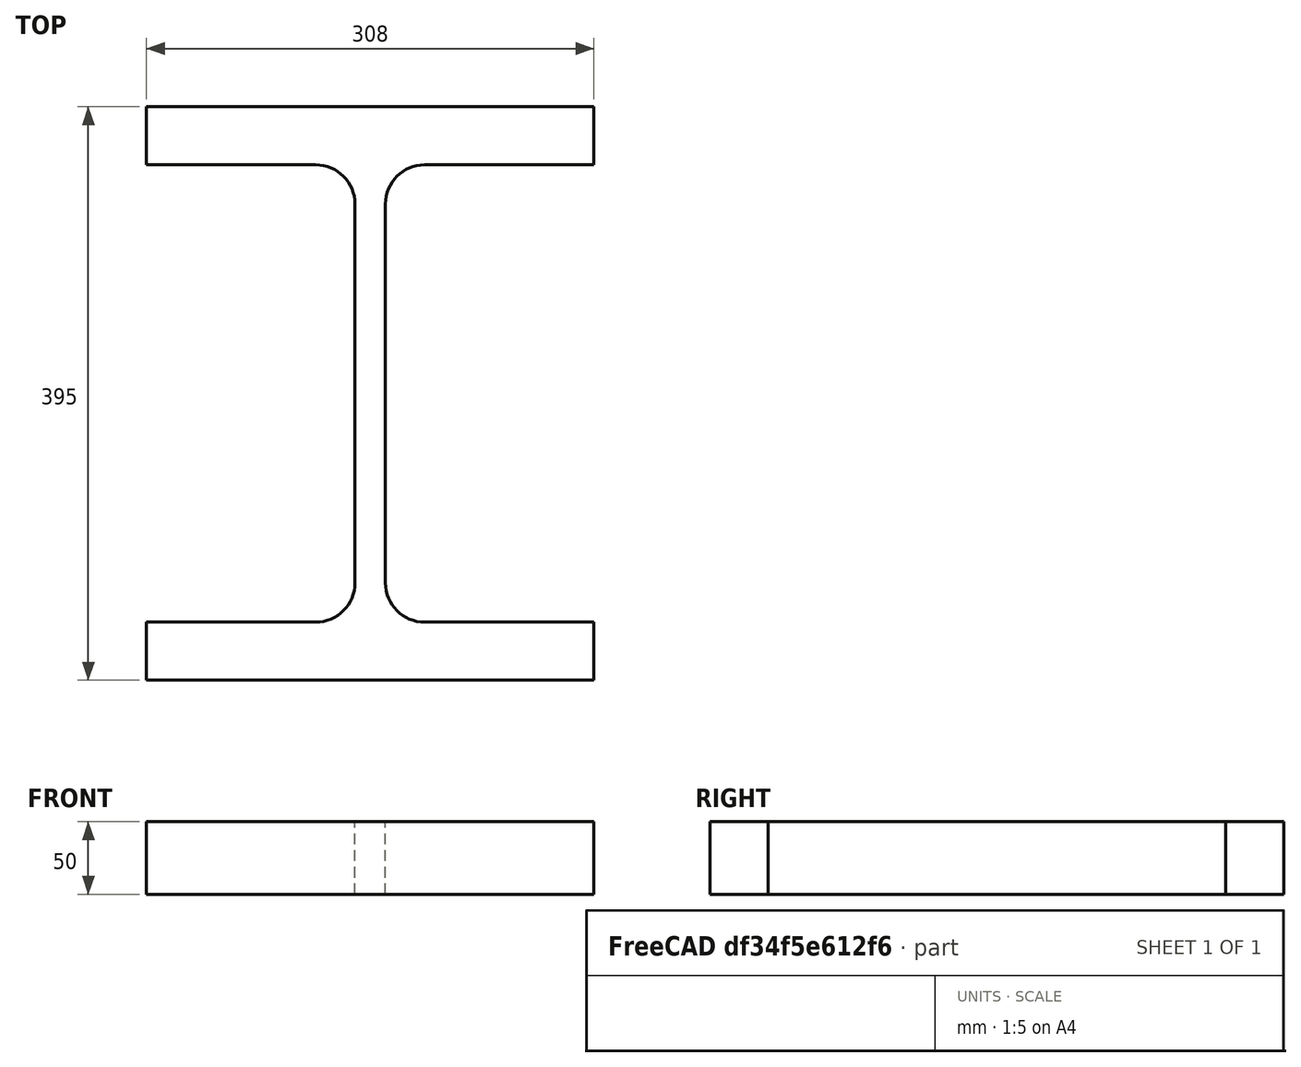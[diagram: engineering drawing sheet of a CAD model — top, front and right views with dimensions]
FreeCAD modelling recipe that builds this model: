
FCSTD DOCUMENT  (FreeCAD 0.15R4671 (Git))
Label: HE-M-Profile 360 DIN1025-4 S235JR
License: All rights reserved
LicenseURL: http://en.wikipedia.org/wiki/All_rights_reserved
objects: Sketcher::SketchObject×1, Part::Extrusion×1
note: 2 computed .brp shape members not serialized (recipe doc carries the construction recipe); baked Part::Feature solids carry a one-line shape summary decoded from their .brp

FEATURE [Sketcher::SketchObject] Sketch
  sketch-geometry (16):
    g0: LineSegment StartX=10.5 StartY=-130.5 StartZ=0 EndX=10.5 EndY=130.5 EndZ=0
    g1: LineSegment StartX=37.5 StartY=157.5 StartZ=0 EndX=154 EndY=157.5 EndZ=0
    g2: LineSegment StartX=154 StartY=157.5 StartZ=0 EndX=154 EndY=197.5 EndZ=0
    g3: LineSegment StartX=154 StartY=197.5 StartZ=0 EndX=-154 EndY=197.5 EndZ=0
    g4: LineSegment StartX=-154 StartY=197.5 StartZ=0 EndX=-154 EndY=157.5 EndZ=0
    g5: LineSegment StartX=-154 StartY=157.5 StartZ=0 EndX=-37.5 EndY=157.5 EndZ=0
    g6: LineSegment StartX=-10.5 StartY=130.5 StartZ=0 EndX=-10.5 EndY=-130.5 EndZ=0
    g7: LineSegment StartX=-37.5 StartY=-157.5 StartZ=0 EndX=-154 EndY=-157.5 EndZ=0
    g8: LineSegment StartX=-154 StartY=-157.5 StartZ=0 EndX=-154 EndY=-197.5 EndZ=0
    g9: LineSegment StartX=-154 StartY=-197.5 StartZ=0 EndX=154 EndY=-197.5 EndZ=0
    g10: LineSegment StartX=154 StartY=-197.5 StartZ=0 EndX=154 EndY=-157.5 EndZ=0
    g11: LineSegment StartX=154 StartY=-157.5 StartZ=0 EndX=37.5 EndY=-157.5 EndZ=0
    g12: ArcOfCircle CenterX=37.5 CenterY=130.5 CenterZ=0 NormalX=0 NormalY=0 NormalZ=1 Radius=27 StartAngle=1.5708 EndAngle=3.14159
    g13: ArcOfCircle CenterX=37.5 CenterY=-130.5 CenterZ=0 NormalX=0 NormalY=0 NormalZ=1 Radius=27 StartAngle=3.14159 EndAngle=4.71239
    g14: ArcOfCircle CenterX=-37.5 CenterY=130.5 CenterZ=0 NormalX=0 NormalY=0 NormalZ=1 Radius=27 StartAngle=0 EndAngle=1.5708
    g15: ArcOfCircle CenterX=-37.5 CenterY=-130.5 CenterZ=0 NormalX=0 NormalY=0 NormalZ=1 Radius=27 StartAngle=4.71239 EndAngle=6.28319
  constraints (42):
    c: Vertical(g0)
    c: Coincident(g2,g1)
    c: Vertical(g2)
    c: Coincident(g3,g2)
    c: Coincident(g4,g3)
    c: Vertical(g4)
    c: Coincident(g5,g4)
    c: Horizontal(g5)
    c: Vertical(g6)
    c: Horizontal(g7)
    c: Coincident(g8,g7)
    c: Vertical(g8)
    c: Coincident(g9,g8)
    c: Horizontal(g9)
    c: Coincident(g10,g9)
    c: Vertical(g10)
    c: Coincident(g11,g10)
    c: Horizontal(g11)
    c: Tangent(g1,g12) = 1.5708
    c: Tangent(g0,g12) = 1.5708
    c: Tangent(g0,g13) = 1.5708
    c: Tangent(g11,g13) = 1.5708
    c: Tangent(g5,g14) = 1.5708
    c: Tangent(g6,g14) = 1.5708
    c: Tangent(g6,g15) = 1.5708
    c: Tangent(g7,g15) = 1.5708
    c: Equal(g3,g9)
    c: Equal(g2,g4)
    c: Equal(g4,g8)
    c: Equal(g8,g10)
    c: Equal(g12,g14)
    c: Equal(g14,g15)
    c: Equal(g15,g13)
    c: Symmetric(g2,g3,g-2)
    c: Symmetric(g9,g8,g-2)
    c: Symmetric(g0,g6,g-2)
    c: Symmetric(g2,g9,g-1)
    c: DistanceY(g2,g9) = -395
    c: DistanceX(g3) = -308
    c: DistanceX(g0,g6) = -21
    c: DistanceY(g2) = 40
    c: Radius(g12) = 27
FEATURE [Part::Extrusion] Extrude  label="HE-M-Profile 360 DIN1025-4 S235JR"
  Base = -> Sketch
  Dir = (0,0,50)
  Solid = true
